# Revit family: Body_Spray-DXV-D357004X0_Series
name_source: partatom
category: Plumbing Fixtures
units: mm (PartAtom-declared; Revit-internal decimal feet)

## family parameters
Cut with Voids When Loaded = No
Host = Face
OmniClass Number = 23.45.05.14.21.17
OmniClass Title = Therapeutic Whirlpool Baths
Part Type = Normal
Room Calculation Point = No
Round Connector Dimension = Use Diameter
Shared = Yes

## types (3) — shared parameters
ASME A112.18.1/CSA B125.1 = Yes
Assembly Code = D2010710
CW Connection = No
CWFU = 3
Default Elevation = 0"
Depth Range = 3 3/4"
Depth Range Constraint = 3 3/4"
Description = Square Multifunction Body Spray
Flow Rate = 2.0 gpm (7.6 L/min)
HW Connection = No
HWFU = 3
Height = 3 3/8"
Installation Type = Wall Mounted
Length = 3/8"
Manufacturer = DXV
Price = Prices may vary. Please consult Manufacturer Representative for most up-to-date price list.
Product Documentation Link = https://dxv01.blob.core.windows.net
Product Page URL = https://www.dxv.com
Revised Date = 02/04/2022
Tempered Water Connection = Yes
Tempered Water Connection Diameter = 1/2"
Tempered Water Connection Radius = 1/4"
URL = https://www.dxv.com
Vent Connection = No
WFU = 4
Warranty Documentation Link = https://www.dxv.com
Waste Connection = No
Width = 3 3/8"

## per-type parameters (varying)
| type | Finish | Material |
| D35700410.100 | Cast Brass-DXV-100-Polished Chrome | Cast Brass-DXV-100-Polished Chrome |
| D35700410.144 | Cast Brass-DXV-144-Brushed Nickel | Cast Brass-DXV-144-Brushed Nickel |
| D35700410.150 | Cast Brass-DXV-150-Platinum Nickel | Cast Brass-DXV-150-Platinum Nickel |

note: column(s) folded — value = type name in every type: Model

## geometry (parser evidence)
native form markers: Sweep x2
no freeform markers — native parametric forms only
